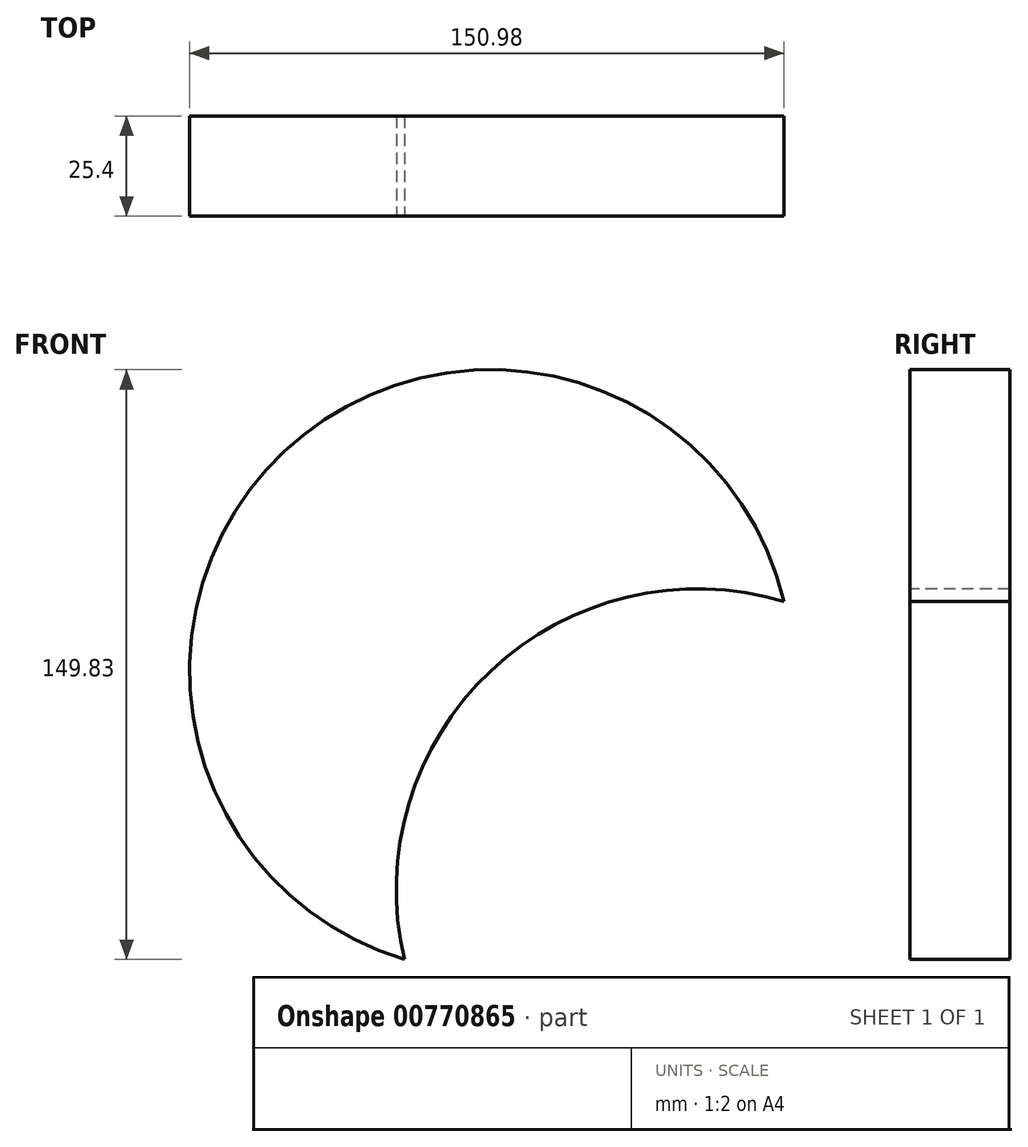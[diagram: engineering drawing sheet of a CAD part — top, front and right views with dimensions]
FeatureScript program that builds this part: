
annotation { "Feature Type Name" : "Feature", "Feature Type Description" : "" }
export const myFeature = defineFeature(function(context is Context, id is Id, definition is map)
    precondition{}
    {
        {
            var Q0;
            Q0=qCreatedBy(makeId("Front.planeOp"),FACE);
            var sketch = newSketch(context, id + "F0", { "sketchPlane" : qUnion([Q0])});
            skCircle(sketch, "E0", {"center": v(-52.5, 55.66) * mm, "radius": 76.52 * mm});
            skCircle(sketch, "E1", {"center": v(0, 0) * mm, "radius": 76.52 * mm});
            skSolve(sketch);
        }
        {
            var Q0;
            {var subQ0=sQuery(id+"F0.wireOp",EDGE,"E1");var subQ1=sQuery(id+"F0.wireOp",EDGE,"E0");var subQ2=makeQuery(id+"F0.imprint","INTERSECT",VERTEX,{"disambiguationData":[OD(0.0)],"derivedFrom":[subQ1,subQ0]});Q0=makeQuery(id+"F0.imprint","IMPRINT",FACE,{"disambiguationData":[TD([[makeQuery(id+"F0.imprint","IMPRINT",EDGE,{"disambiguationData":[TD([[subQ2,1.0]])],"derivedFrom":subQ1}),1.0]])]});}
            extrude(context, id + "F1", {"entities" : qUnion([Q0]), "oppositeDirection" : true, "depth" : 25.4 * mm, "offsetDistance" : 25.4 * mm});
        }
    });
